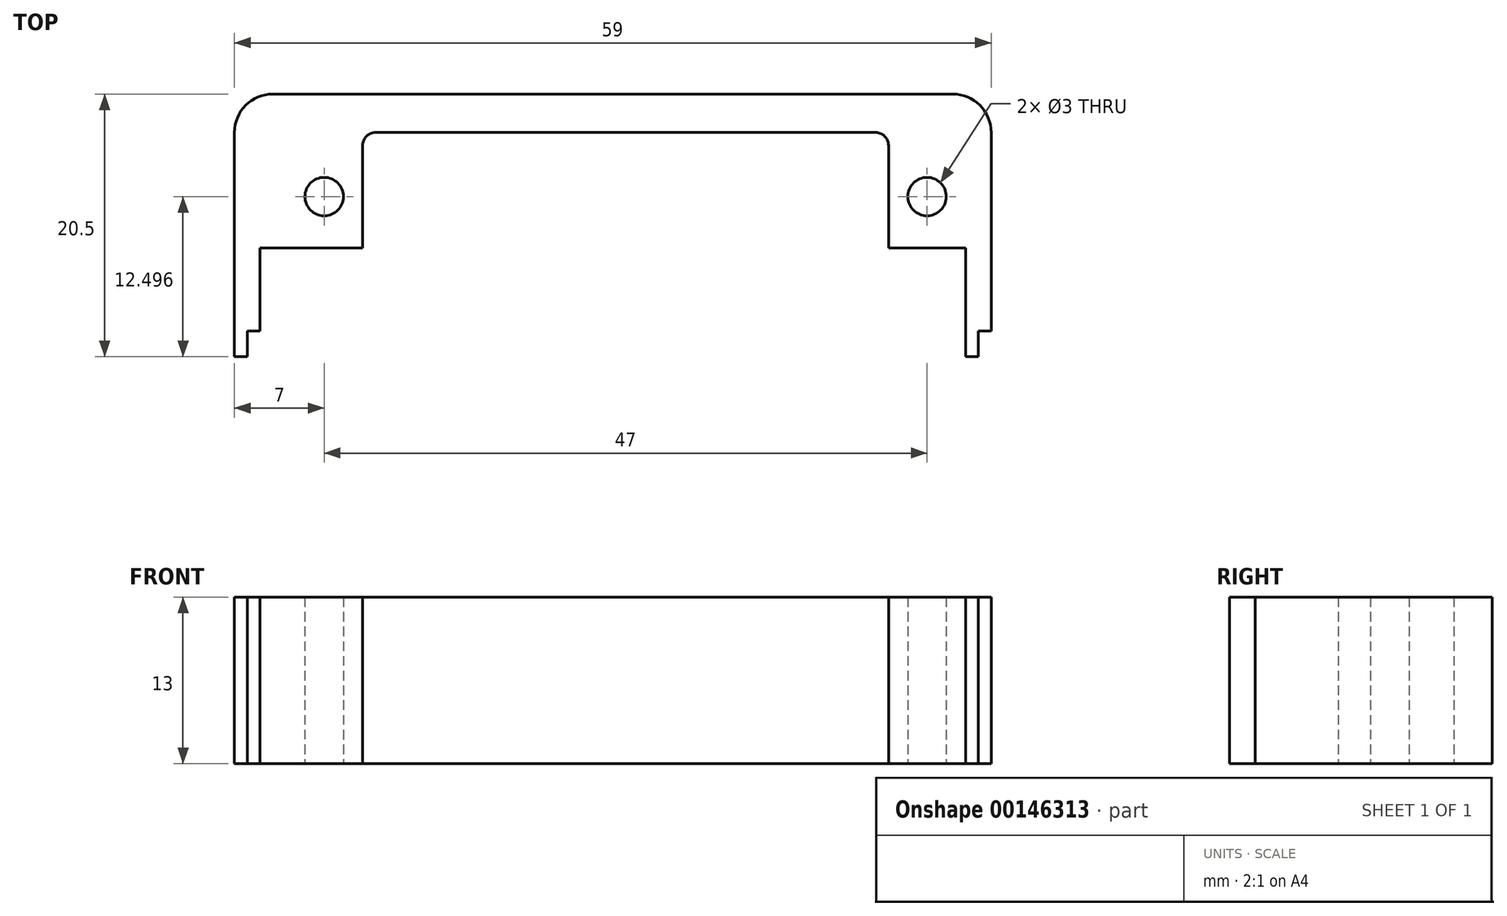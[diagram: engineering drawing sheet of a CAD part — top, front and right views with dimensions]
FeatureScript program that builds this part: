
annotation { "Feature Type Name" : "Feature", "Feature Type Description" : "" }
export const myFeature = defineFeature(function(context is Context, id is Id, definition is map)
    precondition{}
    {
        {
            var Q0;
            Q0=qCreatedBy(makeId("Top.planeOp"),FACE);
            var sketch = newSketch(context, id + "F0", { "sketchPlane" : qUnion([Q0])});
            skLineSegment(sketch, "E0.bottom", {"start": v(-32.43, 9.5) * mm, "end": v(22.57, 9.5) * mm, "construction": true});
            skLineSegment(sketch, "E0.top", {"start": v(-32.43, -25.5) * mm, "end": v(22.57, -25.5) * mm, "construction": true});
            skLineSegment(sketch, "E0.left", {"start": v(-32.43, 9.5) * mm, "end": v(-32.43, -25.5) * mm, "construction": true});
            skLineSegment(sketch, "E0.right", {"start": v(22.57, 9.5) * mm, "end": v(22.57, -25.5) * mm, "construction": true});
            skLineSegment(sketch, "E1.0", {"start": v(-23.43, 8.5) * mm, "end": v(15.57, 8.5) * mm});
            skLineSegment(sketch, "E2.0", {"start": v(-25.43, -24.5) * mm, "end": v(13.57, -24.5) * mm});
            skLineSegment(sketch, "E3.0", {"start": v(-24.43, -13.5) * mm, "end": v(12.57, -13.5) * mm});
            skLineSegment(sketch, "E4.0", {"start": v(-22.43, -2.5) * mm, "end": v(14.57, -2.5) * mm});
            skLineSegment(sketch, "E5.0", {"start": v(-26.43, -15.5) * mm, "end": v(-26.43, -23.5) * mm});
            skLineSegment(sketch, "E6.0", {"start": v(16.57, 7.5) * mm, "end": v(16.57, -0.5) * mm});
            skLineSegment(sketch, "E7.0", {"start": v(-31.43, -27.5) * mm, "end": v(21.57, -27.5) * mm});
            skLineSegment(sketch, "E8.0", {"start": v(-31.43, 11.5) * mm, "end": v(21.57, 11.5) * mm});
            skLineSegment(sketch, "E9.0", {"start": v(14.57, -15.5) * mm, "end": v(14.57, -23.5) * mm});
            skLineSegment(sketch, "E10.0", {"start": v(-24.43, 7.5) * mm, "end": v(-24.43, -0.5) * mm});
            skArc(sketch, "E11.filletArc", {"start": v(14.57, -15.5) * mm, "mid": v(13.98, -14.09) * mm, "end": v(12.57, -13.5) * mm});
            skArc(sketch, "E12.filletArc", {"start": v(13.57, -24.5) * mm, "mid": v(14.28, -24.21) * mm, "end": v(14.57, -23.5) * mm});
            skArc(sketch, "E13.filletArc", {"start": v(-26.43, -23.5) * mm, "mid": v(-26.14, -24.21) * mm, "end": v(-25.43, -24.5) * mm});
            skArc(sketch, "E14.filletArc", {"start": v(-24.43, -13.5) * mm, "mid": v(-25.84, -14.09) * mm, "end": v(-26.43, -15.5) * mm});
            skArc(sketch, "E15.filletArc", {"start": v(-24.43, -0.5) * mm, "mid": v(-23.84, -1.92) * mm, "end": v(-22.43, -2.5) * mm});
            skArc(sketch, "E16.filletArc", {"start": v(-23.43, 8.5) * mm, "mid": v(-24.14, 8.2) * mm, "end": v(-24.43, 7.5) * mm});
            skArc(sketch, "E17.filletArc", {"start": v(14.57, -2.5) * mm, "mid": v(15.98, -1.92) * mm, "end": v(16.57, -0.5) * mm});
            skArc(sketch, "E18.filletArc", {"start": v(16.57, 7.5) * mm, "mid": v(16.28, 8.2) * mm, "end": v(15.57, 8.5) * mm});
            skLineSegment(sketch, "E19", {"start": v(-32.43, 3.5) * mm, "end": v(22.57, 3.5) * mm, "construction": true});
            skPoint(sketch, "E19.startSnap0", {"position": v(-24.43, 3.5) * mm});
            skPoint(sketch, "E19.endSnap0", {"position": v(16.57, 3.5) * mm});
            skLineSegment(sketch, "E20", {"start": v(-32.43, -19.5) * mm, "end": v(22.57, -19.5) * mm, "construction": true});
            skPoint(sketch, "E20.startSnap0", {"position": v(-26.43, -19.5) * mm});
            skLineSegment(sketch, "E21.0", {"start": v(-29.43, 9.5) * mm, "end": v(-29.43, -25.5) * mm, "construction": true});
            skLineSegment(sketch, "E22.0", {"start": v(19.57, 9.5) * mm, "end": v(19.57, -25.5) * mm, "construction": true});
            skLineSegment(sketch, "E23.0", {"start": v(-27.43, 7.5) * mm, "end": v(-27.43, -0.5) * mm, "construction": true});
            skLineSegment(sketch, "E24.0", {"start": v(17.57, -15.5) * mm, "end": v(17.57, -23.5) * mm, "construction": true});
            skCircle(sketch, "E25", {"center": v(-29.43, -19.5) * mm, "radius": 1.5 * mm});
            skCircle(sketch, "E26", {"center": v(-27.43, 3.5) * mm, "radius": 1.5 * mm});
            skCircle(sketch, "E27", {"center": v(19.57, 3.5) * mm, "radius": 1.5 * mm});
            skCircle(sketch, "E28", {"center": v(17.57, -19.5) * mm, "radius": 1.5 * mm});
            skLineSegment(sketch, "E29.0", {"start": v(24.57, 8.5) * mm, "end": v(24.57, -24.5) * mm});
            skLineSegment(sketch, "E30.0", {"start": v(-34.43, 8.5) * mm, "end": v(-34.43, -24.5) * mm});
            skLineSegment(sketch, "E31", {"start": v(-26.43, -15.5) * mm, "end": v(-32.43, -15.5) * mm});
            skLineSegment(sketch, "E32", {"start": v(-32.43, -15.5) * mm, "end": v(-32.43, -0.5) * mm});
            skLineSegment(sketch, "E33", {"start": v(-32.43, -0.5) * mm, "end": v(-24.43, -0.5) * mm});
            skLineSegment(sketch, "E34", {"start": v(22.57, -15.91) * mm, "end": v(22.57, -0.5) * mm});
            skLineSegment(sketch, "E35", {"start": v(22.57, -0.5) * mm, "end": v(16.57, -0.5) * mm});
            skPoint(sketch, "E36.visualSharp", {"position": v(-34.43, -27.5) * mm});
            skArc(sketch, "E36.filletArc", {"start": v(-34.43, -24.5) * mm, "mid": v(-33.55, -26.63) * mm, "end": v(-31.43, -27.5) * mm});
            skPoint(sketch, "E37.visualSharp", {"position": v(-34.43, 11.5) * mm});
            skArc(sketch, "E37.filletArc", {"start": v(-31.43, 11.5) * mm, "mid": v(-33.55, 10.62) * mm, "end": v(-34.43, 8.5) * mm});
            skPoint(sketch, "E38.visualSharp", {"position": v(24.57, 11.5) * mm});
            skArc(sketch, "E38.filletArc", {"start": v(24.57, 8.5) * mm, "mid": v(23.7, 10.62) * mm, "end": v(21.57, 11.5) * mm});
            skPoint(sketch, "E39.visualSharp", {"position": v(24.57, -27.5) * mm});
            skArc(sketch, "E39.filletArc", {"start": v(21.57, -27.5) * mm, "mid": v(23.7, -26.63) * mm, "end": v(24.57, -24.5) * mm});
            skLineSegment(sketch, "E40", {"start": v(14.57, -15.5) * mm, "end": v(22.57, -15.5) * mm});
            skLineSegment(sketch, "E41", {"start": v(-32.43, -8) * mm, "end": v(-34.43, -8) * mm, "construction": true});
            skLineSegment(sketch, "E42", {"start": v(24.57, -8) * mm, "end": v(22.57, -8) * mm, "construction": true});
            skLineSegment(sketch, "E43", {"start": v(-34.43, -9) * mm, "end": v(-33.43, -9) * mm});
            skLineSegment(sketch, "E44", {"start": v(-33.43, -9) * mm, "end": v(-33.43, -7) * mm});
            skLineSegment(sketch, "E45", {"start": v(-33.43, -7) * mm, "end": v(-32.43, -7) * mm});
            skLineSegment(sketch, "E46.0", {"start": v(24.57, -7) * mm, "end": v(23.57, -7) * mm});
            skLineSegment(sketch, "E47.0", {"start": v(23.57, -9) * mm, "end": v(22.57, -9) * mm});
            skLineSegment(sketch, "E48", {"start": v(23.57, -7) * mm, "end": v(23.57, -9) * mm});
            skPoint(sketch, "E49.orphan", {"position": v(24.57, -9) * mm});
            skPoint(sketch, "E50.orphan", {"position": v(22.57, -7) * mm});
            skSolve(sketch);
        }
        {
            var Q0;
            Q0=makeQuery(id+"F0.imprint","IMPRINT",FACE,{"disambiguationData":[TD([[makeQuery(id+"F0.imprint","IMPRINT",EDGE,{"derivedFrom":sQuery(id+"F0.wireOp",EDGE,"E1.0")}),1.0]])]});
            extrude(context, id + "F1", {"entities" : qUnion([Q0]), "depth" : 13 * mm});
        }
    });
